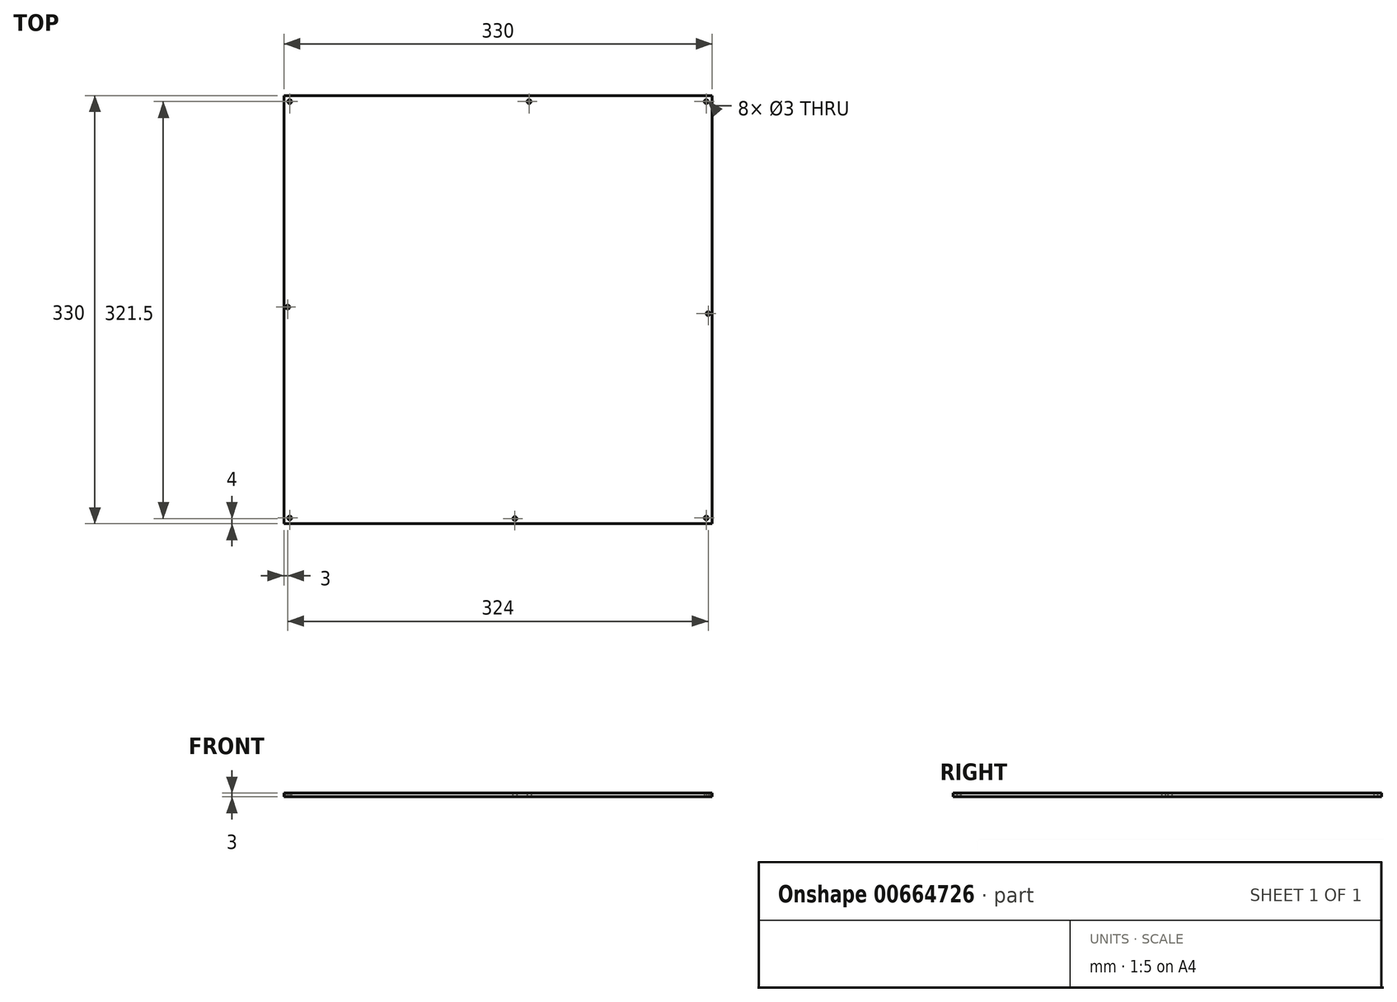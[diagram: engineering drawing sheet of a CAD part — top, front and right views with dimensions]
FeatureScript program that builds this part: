
annotation { "Feature Type Name" : "Feature", "Feature Type Description" : "" }
export const myFeature = defineFeature(function(context is Context, id is Id, definition is map)
    precondition{}
    {
        {
            var Q0;
            Q0=qCreatedBy(makeId("Top.planeOp"),FACE);
            var sketch = newSketch(context, id + "F0", { "sketchPlane" : qUnion([Q0])});
            skLineSegment(sketch, "E0.bottom", {"start": v(165, 165) * mm, "end": v(-165, 165) * mm});
            skLineSegment(sketch, "E0.top", {"start": v(165, -165) * mm, "end": v(-165, -165) * mm});
            skLineSegment(sketch, "E0.left", {"start": v(165, 165) * mm, "end": v(165, -165) * mm});
            skLineSegment(sketch, "E0.right", {"start": v(-165, 165) * mm, "end": v(-165, -165) * mm});
            skPoint(sketch, "E0.middle", {"position": v(0, 0) * mm});
            skCircle(sketch, "E1", {"center": v(160.5, 160.5) * mm, "radius": 1.5 * mm});
            skCircle(sketch, "E2", {"center": v(160.5, -160.5) * mm, "radius": 1.5 * mm});
            skCircle(sketch, "E3", {"center": v(-160.5, 160.5) * mm, "radius": 1.5 * mm});
            skCircle(sketch, "E4", {"center": v(-160.5, -160.5) * mm, "radius": 1.5 * mm});
            skCircle(sketch, "E5", {"center": v(24, 160.5) * mm, "radius": 1.5 * mm});
            skCircle(sketch, "E6", {"center": v(162, -3) * mm, "radius": 1.5 * mm});
            skCircle(sketch, "E7", {"center": v(-162, 2) * mm, "radius": 1.5 * mm});
            skCircle(sketch, "E8", {"center": v(13, -161) * mm, "radius": 1.5 * mm});
            skSolve(sketch);
        }
        {
            var Q0;
            Q0=makeQuery(id+"F0.imprint","IMPRINT",FACE,{"disambiguationData":[TD([[makeQuery(id+"F0.imprint","IMPRINT",EDGE,{"derivedFrom":sQuery(id+"F0.wireOp",EDGE,"E0.bottom")}),1.0]])]});
            extrude(context, id + "F1", {"entities" : qUnion([Q0]), "depth" : 3 * mm, "offsetDistance" : 25 * mm});
        }
        {
            var Q0;
            Q0=makeQuery(id+"F1.opExtrude","CAP_FACE",FACE,{"disambiguationData":[OSD([sQuery(id+"F0.wireOp",EDGE,"E0.bottom"),sQuery(id+"F0.wireOp",EDGE,"E0.top"),sQuery(id+"F0.wireOp",EDGE,"E0.left"),sQuery(id+"F0.wireOp",EDGE,"E0.right"),sQuery(id+"F0.wireOp",EDGE,"E1"),sQuery(id+"F0.wireOp",EDGE,"E2"),sQuery(id+"F0.wireOp",EDGE,"E3"),sQuery(id+"F0.wireOp",EDGE,"E4"),sQuery(id+"F0.wireOp",EDGE,"E5"),sQuery(id+"F0.wireOp",EDGE,"E6"),sQuery(id+"F0.wireOp",EDGE,"E7"),sQuery(id+"F0.wireOp",EDGE,"E8")])],"isStart":false});
            cPlane(context, id + "F2", {"entities" : qUnion([Q0]), "cplaneType" : CPlaneType.OFFSET, "offset" : 0 * mm, "width" : 150 * mm, "height" : 150 * mm});
        }
    });
